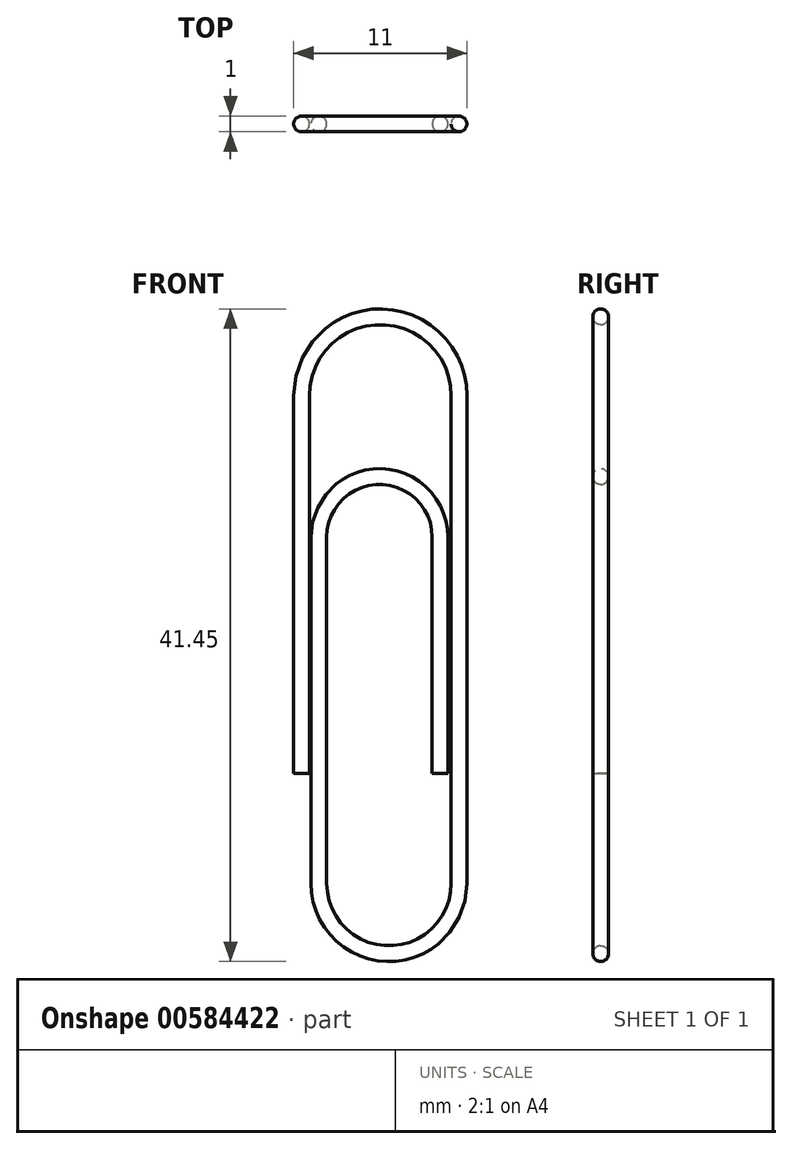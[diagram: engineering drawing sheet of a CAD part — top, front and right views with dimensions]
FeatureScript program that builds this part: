
annotation { "Feature Type Name" : "Feature", "Feature Type Description" : "" }
export const myFeature = defineFeature(function(context is Context, id is Id, definition is map)
    precondition{}
    {
        {
            var Q0;
            Q0=qCreatedBy(makeId("Front.planeOp"),FACE);
            var sketch = newSketch(context, id + "F0", { "sketchPlane" : qUnion([Q0])});
            skLineSegment(sketch, "E0", {"start": v(0, 0) * mm, "end": v(0, 24) * mm});
            skLineSegment(sketch, "E1", {"start": v(10, 24) * mm, "end": v(10, -7) * mm});
            skLineSegment(sketch, "E2", {"start": v(1.1, -7) * mm, "end": v(1.1, 15) * mm});
            skLineSegment(sketch, "E3", {"start": v(8.8, 15) * mm, "end": v(8.8, 0) * mm});
            skArc(sketch, "E4", {"start": v(10, 24) * mm, "mid": v(5, 29) * mm, "end": v(0, 24) * mm});
            skArc(sketch, "E5", {"start": v(1.1, -7) * mm, "mid": v(5.55, -11.45) * mm, "end": v(10, -7) * mm});
            skArc(sketch, "E6", {"start": v(8.8, 15) * mm, "mid": v(4.95, 18.85) * mm, "end": v(1.1, 15) * mm});
            skSolve(sketch);
        }
        {
            var Q0;
            Q0=qCreatedBy(makeId("Top.planeOp"),FACE);
            var sketch = newSketch(context, id + "F1", { "sketchPlane" : qUnion([Q0])});
            skCircle(sketch, "E7", {"center": v(0, 0) * mm, "radius": 0.5 * mm});
            skSolve(sketch);
        }
        {
            var Q0;
            Q0 = qSketchRegion(id + "F1", true);
            var Q1;
            Q1 = qConstructionFilter(qBodyType(qCreatedBy(id + "F0" ,EDGE), BodyType.WIRE), ConstructionObject.NO);
            sweep(context, id + "F2", {"profiles" : qUnion([Q0]), "path" : qUnion([Q1])});
        }
    });
